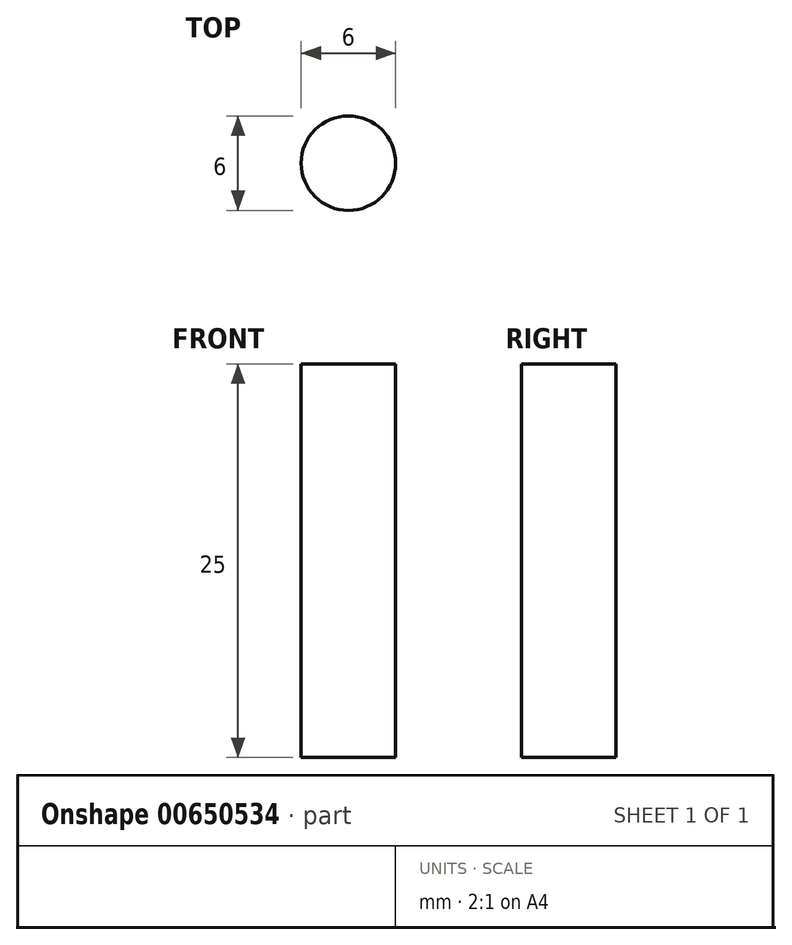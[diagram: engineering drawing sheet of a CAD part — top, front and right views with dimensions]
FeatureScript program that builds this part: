
annotation { "Feature Type Name" : "Feature", "Feature Type Description" : "" }
export const myFeature = defineFeature(function(context is Context, id is Id, definition is map)
    precondition{}
    {
        {
            var Q0;
            Q0=qCreatedBy(makeId("Top.planeOp"),FACE);
            var sketch = newSketch(context, id + "F0", { "sketchPlane" : qUnion([Q0])});
            skCircle(sketch, "E0", {"center": v(0, 0) * mm, "radius": 3 * mm});
            skSolve(sketch);
        }
        {
            var Q0;
            Q0=makeQuery(id+"F0.imprint","IMPRINT",FACE,{"disambiguationData":[TD([[makeQuery(id+"F0.imprint","IMPRINT",EDGE,{"derivedFrom":sQuery(id+"F0.wireOp",EDGE,"E0")}),1.0]])]});
            extrude(context, id + "F1", {"entities" : qUnion([Q0]), "endBound" : BoundingType.SYMMETRIC, "depth" : 25 * mm, "offsetDistance" : 25 * mm});
        }
    });
